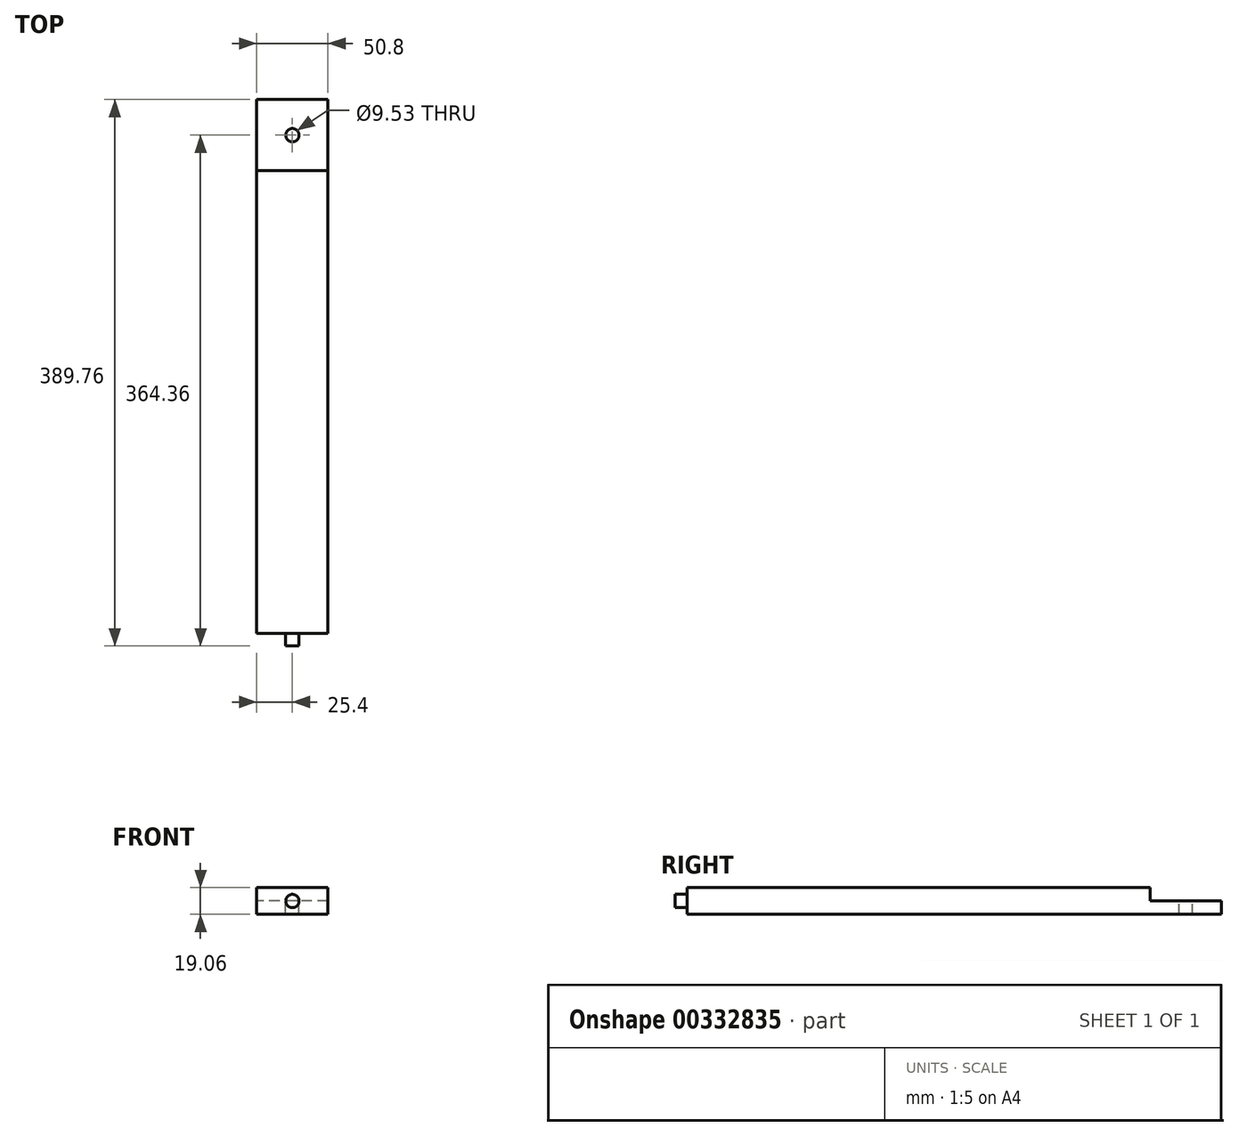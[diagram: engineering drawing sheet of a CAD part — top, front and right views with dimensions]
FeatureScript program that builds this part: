
annotation { "Feature Type Name" : "Feature", "Feature Type Description" : "" }
export const myFeature = defineFeature(function(context is Context, id is Id, definition is map)
    precondition{}
    {
        {
            var Q0;
            Q0=qCreatedBy(makeId("Right.planeOp"),FACE);
            var sketch = newSketch(context, id + "F0", { "sketchPlane" : qUnion([Q0])});
            skLineSegment(sketch, "E0.right", {"start": v(-19.82, 9.52) * mm, "end": v(310.38, 9.53) * mm});
            skLineSegment(sketch, "E1", {"start": v(361.18, -9.52) * mm, "end": v(-19.82, -9.53) * mm});
            skLineSegment(sketch, "E2.top", {"start": v(310.38, 9.53) * mm, "end": v(310.38, 0) * mm});
            skLineSegment(sketch, "E2.right", {"start": v(361.18, 0) * mm, "end": v(310.38, 0) * mm});
            skLineSegment(sketch, "E3", {"start": v(361.18, 0) * mm, "end": v(361.18, -9.52) * mm});
            skPoint(sketch, "E4.orphan", {"position": v(0, 9.52) * mm});
            skLineSegment(sketch, "E5", {"start": v(-19.82, 9.52) * mm, "end": v(-19.82, -9.53) * mm});
            skPoint(sketch, "E6.end.orphan", {"position": v(-38.87, -9.53) * mm});
            skSolve(sketch);
        }
        {
            var Q0;
            Q0=qSketchRegion(id+"F0",true);
            extrude(context, id + "F1", {"entities" : qUnion([Q0]), "endBound" : BoundingType.SYMMETRIC, "depth" : 50.8 * mm});
        }
        {
            var Q0;
            Q0=qCreatedBy(makeId("Top.planeOp"),FACE);
            var sketch = newSketch(context, id + "F2", { "sketchPlane" : qUnion([Q0])});
            skCircle(sketch, "E7", {"center": v(0, 335.78) * mm, "radius": 4.76 * mm});
            skSolve(sketch);
        }
        {
            var Q0;
            Q0 = qSketchRegion(id + "F2", true);
            extrude(context, id + "F3", {"entities" : qUnion([Q0]), "operationType" : NewBodyOperationType.REMOVE, "oppositeDirection" : true, "depth" : 25.4 * mm});
        }
        {
            var Q0;
            Q0=qCreatedBy(makeId("Front.planeOp"),FACE);
            cPlane(context, id + "F4", {"entities" : qUnion([Q0]), "cplaneType" : CPlaneType.OFFSET, "offset" : 19.05 * mm, "width" : 152.4 * mm, "height" : 152.4 * mm});
        }
        {
            var Q0;
            Q0=qCreatedBy(id+"F4.planeOp",FACE);
            var sketch = newSketch(context, id + "F5", { "sketchPlane" : qUnion([Q0])});
            skCircle(sketch, "E8", {"center": v(0, 0) * mm, "radius": 4.76 * mm});
            skSolve(sketch);
        }
        {
            var Q0;
            Q0 = qSketchRegion(id + "F5", true);
            extrude(context, id + "F6", {"entities" : qUnion([Q0]), "operationType" : NewBodyOperationType.ADD, "depth" : 9.52 * mm});
        }
    });
